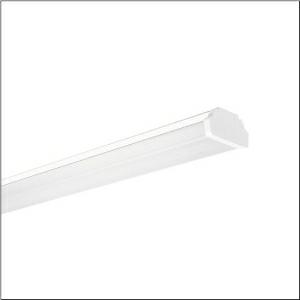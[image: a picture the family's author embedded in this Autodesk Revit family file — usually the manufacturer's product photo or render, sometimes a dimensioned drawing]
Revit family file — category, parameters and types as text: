
# Revit family: dus_r__31_ho_53bd812d2v4120_dd06
name_source: partatom
category: Lighting Fixtures
units: mm (PartAtom-declared; Revit-internal decimal feet)

## family parameters
Cut with Voids When Loaded = No
Host = Face
Light Source = No
Part Type = Normal
Room Calculation Point = No
Round Connector Dimension = Use Diameter
Shared = No

## types (1)
- --- (1 x LED, 12350 lm, 79.5 W, 4000K)
    Apparent Load = 80 VA
    CIE Flux Codes = 47 80 95 92 100
    Color Rendering = 80
    Color Temperature = 4000K
    Default Elevation = 1800 mm
    Description = DUS® 31 HO, luminaire insert, of sheet steel, coil coated, white, length: 1.535mm, width: 81mm, height: 90mm, 5x system unit, system units: 307mm, LED rated luminous flux: 12.350lm, light colour: 840, control gear: DALI 2, control gear: ECG DALI, with plug, 5-pole, with phase selection, mains connection: 220..240V, AC, 50/60Hz, rated input power: 80W, through-wiring accessed according to module size, primary optical cover: cover, of PMMA, light emission: direct distribution, primary light characteristic: symmetric, protection rating (complete): IP20, protection rating (LED compartment): IP50, insulation class (complete): insulation class I (protective earthing), certification: CE, ENEC, VDE, UKCA, impact resistance: IK03, permissible ambient temperature for indoor applications: -25..+30°C, corresponds to IFS (International Featured Standards) requirements for safety and quality in the food industry, reducing of maximum allowable ambient temperature of 5°C with ceiling mounting, packaging unit: 1 piece
    Height = 95 mm
    Lamp = 1 x LED
    Lamp Light Flux = 12350 lm
    Lamp Power = 79.5 W
    Lamp count = 1
    Length = 1535 mm
    Luminous efficacy = 155 lm/W
    Manufacturer = Siteco
    ModVariant = No
    Model = 53BD812D2V4120
    Mounting Place = Ceiling
    Mounting Type = Pendant
    Number of Poles = 1
    OnlyDefault = Yes
    Power Factor = 1
    Product Name = DUS® 31 HO
    Product group = luminaire insert
    ProductGroupID = 902
    Protection Class = Protection class I
    Protection Degree = IP 20
    RLX_Detail_Level = 1
    RLX_Emergency_Light_Flux = 0 lm
    RLX_Emergency_Type = 0
    RLX_Emergency_Type_DB = No
    RlxData = <blob elided: 42273 chars, md5=76b6cbb2>
    Socket = socket
    Standby Power = 0 W
    System Light Flux = 12350 lm
    System Power = 80 W
    Type Comments = factory setting: luminous flux: 100 % | dim-lin: 254 | 345 mA
    Type Image = l_1319596.jpg
    URL = http://relux.com
    VarID = @adj_199222
    Voltage = 0 V
    Weight = 0.00 kg
    Width = 81 mm

## geometry (parser evidence)
native form markers: Blend x4, Sweep x13
no freeform markers — native parametric forms only
